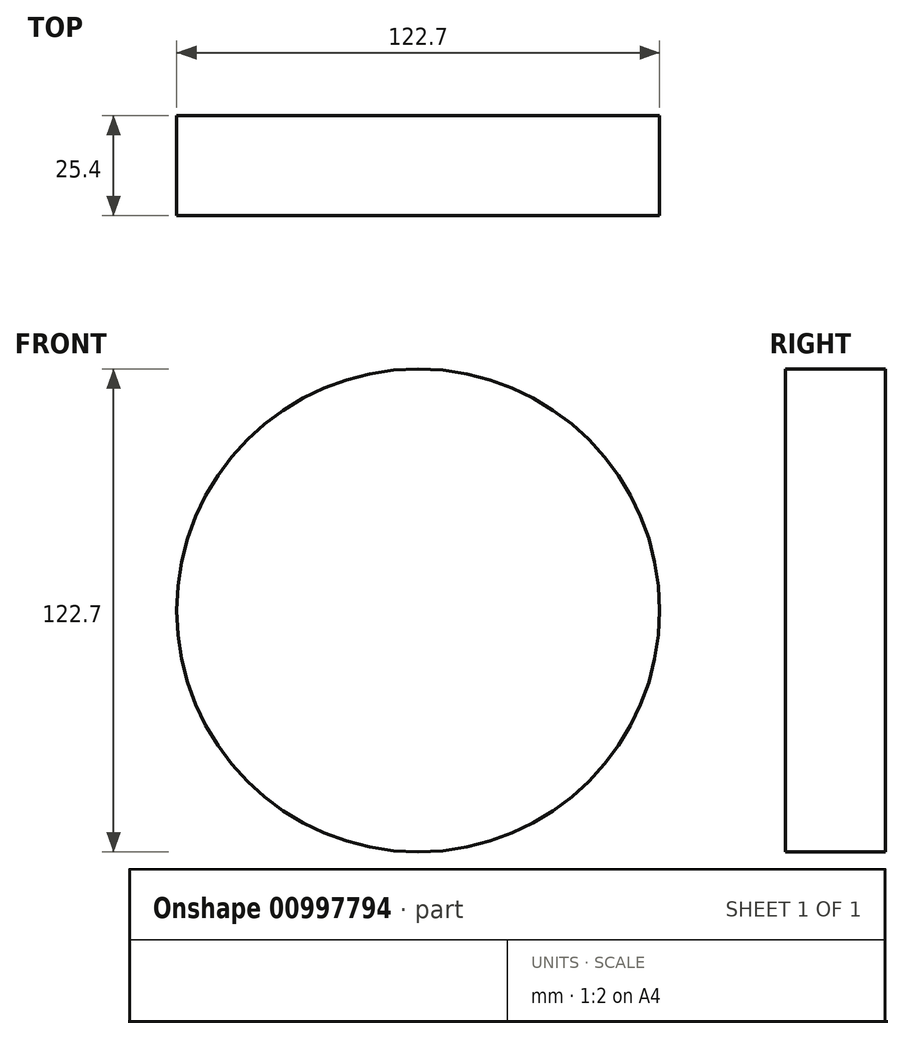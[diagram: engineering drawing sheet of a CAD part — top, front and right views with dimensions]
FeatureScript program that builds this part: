
annotation { "Feature Type Name" : "Feature", "Feature Type Description" : "" }
export const myFeature = defineFeature(function(context is Context, id is Id, definition is map)
    precondition{}
    {
        {
            var Q0;
            Q0=qCreatedBy(makeId("Front.planeOp"),FACE);
            var sketch = newSketch(context, id + "F0", { "sketchPlane" : qUnion([Q0])});
            skCircle(sketch, "E0", {"center": v(0, 0) * mm, "radius": 61.35 * mm});
            skSolve(sketch);
        }
        {
            var Q0;
            Q0=makeQuery(id+"F0.imprint","IMPRINT",FACE,{"disambiguationData":[TD([[makeQuery(id+"F0.imprint","IMPRINT",EDGE,{"derivedFrom":sQuery(id+"F0.wireOp",EDGE,"E0")}),1.0]])]});
            var sketch = newSketch(context, id + "F1", { "sketchPlane" : qUnion([Q0])});
            skSolve(sketch);
        }
        {
            var Q0;
            Q0 = qSketchRegion(id + "F1", true);
            var Q1;
            Q1=makeQuery(id+"F0.imprint","IMPRINT",FACE,{"disambiguationData":[TD([[makeQuery(id+"F0.imprint","IMPRINT",EDGE,{"derivedFrom":sQuery(id+"F0.wireOp",EDGE,"E0")}),1.0]])]});
            extrude(context, id + "F2", {"entities" : qUnion([Q0, Q1]), "depth" : 25.4 * mm, "offsetDistance" : 25.4 * mm});
        }
        {
            var Q0;
            Q0=makeQuery(id+"F1.imprint","IMPRINT",FACE,{"disambiguationData":[TD([[makeQuery(id+"F1.imprint","IMPRINT",EDGE,{"derivedFrom":makeQuery(id+"F0.imprint","IMPRINT",EDGE,{"derivedFrom":sQuery(id+"F0.wireOp",EDGE,"E0")})}),1.0]])]});
            var sketch = newSketch(context, id + "F3", { "sketchPlane" : qUnion([Q0])});
            skLineSegment(sketch, "E1", {"start": v(43.65, 41.64) * mm, "end": v(17.77, 0) * mm});
            skLineSegment(sketch, "E2", {"start": v(31.97, 50.9) * mm, "end": v(2.69, 0) * mm});
            skLineSegment(sketch, "E3", {"start": v(2.69, 0) * mm, "end": v(-32.88, 51.45) * mm});
            skLineSegment(sketch, "E4", {"start": v(-16.8, 0) * mm, "end": v(-47.43, 39.33) * mm});
            skLineSegment(sketch, "E5", {"start": v(17.77, 0) * mm, "end": v(48.14, -38.98) * mm});
            skLineSegment(sketch, "E6", {"start": v(2.69, -8.94) * mm, "end": v(32.83, -48.88) * mm});
            skLineSegment(sketch, "E7", {"start": v(0, -10.7) * mm, "end": v(-26.08, -52.65) * mm});
            skLineSegment(sketch, "E8", {"start": v(-16.8, 0) * mm, "end": v(-43.93, -43.67) * mm});
            skSolve(sketch);
        }
        {
            var Q0;
            Q0 = qSketchRegion(id + "F3", true);
            var Q1;
            Q1=makeQuery(id+"F1.imprint","IMPRINT",FACE,{"disambiguationData":[TD([[makeQuery(id+"F1.imprint","IMPRINT",EDGE,{"derivedFrom":makeQuery(id+"F0.imprint","IMPRINT",EDGE,{"derivedFrom":sQuery(id+"F0.wireOp",EDGE,"E0")})}),1.0]])]});
            extrude(context, id + "F4", {"entities" : qUnion([Q0, Q1]), "operationType" : NewBodyOperationType.ADD, "depth" : 25.4 * mm, "offsetDistance" : 25.4 * mm});
        }
        {
            var Q0;
            Q0=sQuery(id+"F3.wireOp",EDGE,"E7");
            var Q1;
            Q1=sQuery(id+"F3.wireOp",EDGE,"E8");
            var Q2;
            Q2=sQuery(id+"F3.wireOp",EDGE,"E4");
            var Q3;
            Q3=sQuery(id+"F3.wireOp",EDGE,"E3");
            var Q4;
            Q4=sQuery(id+"F3.wireOp",EDGE,"E2");
            var Q5;
            Q5=sQuery(id+"F3.wireOp",EDGE,"E1");
            var Q6;
            Q6=sQuery(id+"F3.wireOp",EDGE,"E5");
            var Q7;
            Q7=sQuery(id+"F3.wireOp",EDGE,"E6");
            extrude(context, id + "F5", {"bodyType" : ToolBodyType.SURFACE, "surfaceEntities" : qUnion([Q0, Q1, Q2, Q3, Q4, Q5, Q6, Q7]), "depth" : 67.06 * mm, "offsetDistance" : 25.4 * mm});
        }
    });
